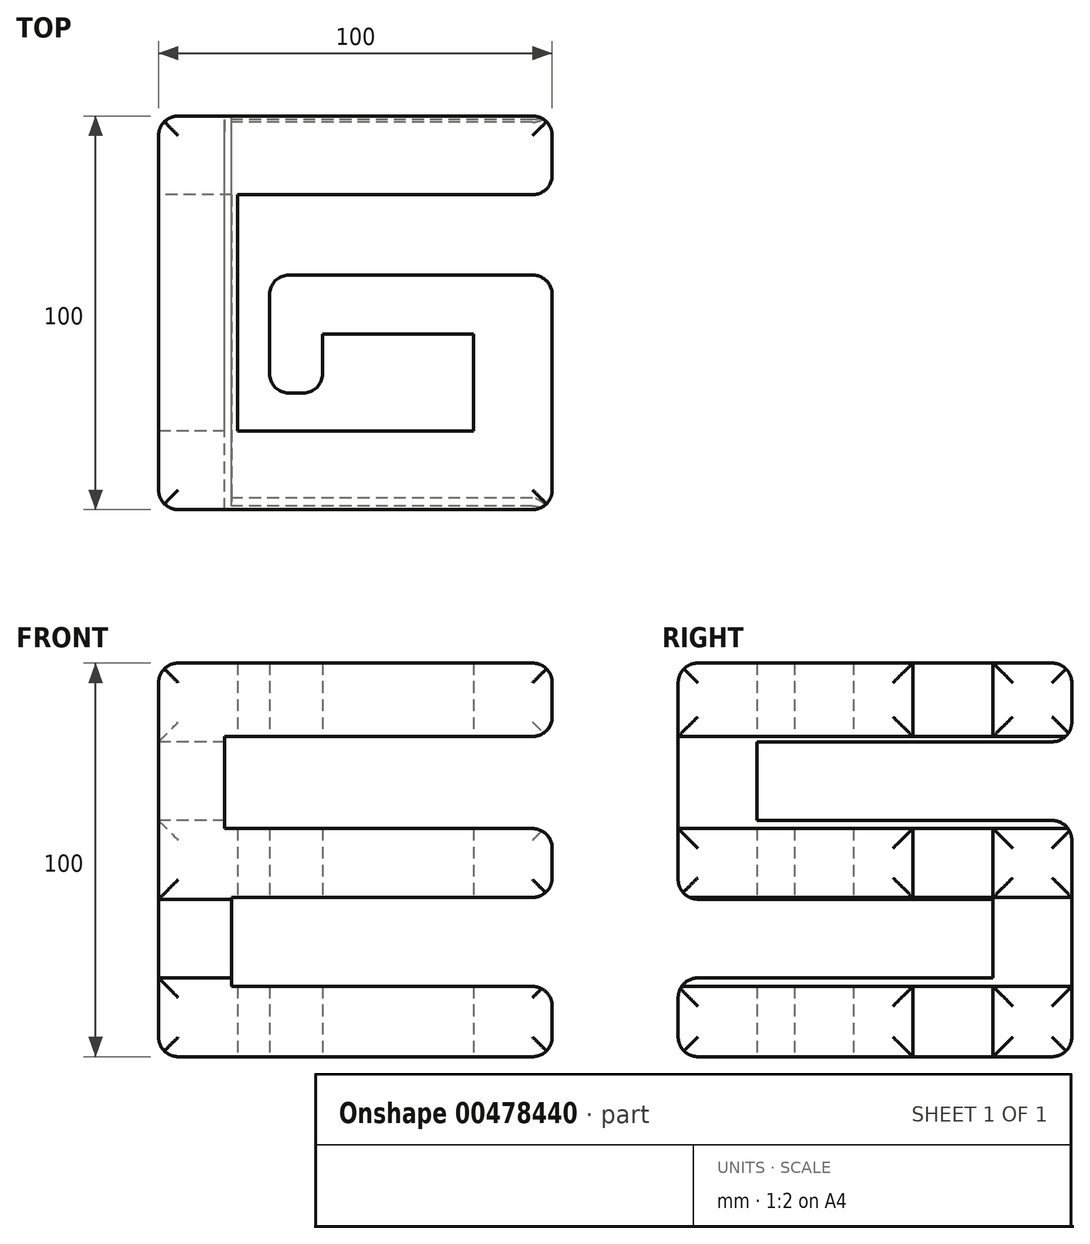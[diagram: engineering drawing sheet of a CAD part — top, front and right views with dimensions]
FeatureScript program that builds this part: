
annotation { "Feature Type Name" : "Feature", "Feature Type Description" : "" }
export const myFeature = defineFeature(function(context is Context, id is Id, definition is map)
    precondition{}
    {
        {
            var Q0;
            Q0=qCreatedBy(makeId("Top.planeOp"),FACE);
            var sketch = newSketch(context, id + "F0", { "sketchPlane" : qUnion([Q0])});
            skLineSegment(sketch, "E0.bottom", {"start": v(50, 50) * mm, "end": v(-50, 50) * mm, "construction": true});
            skLineSegment(sketch, "E0.top", {"start": v(50, -50) * mm, "end": v(-50, -50) * mm, "construction": true});
            skLineSegment(sketch, "E0.left", {"start": v(50, 50) * mm, "end": v(50, -50) * mm, "construction": true});
            skLineSegment(sketch, "E0.right", {"start": v(-50, 50) * mm, "end": v(-50, -50) * mm, "construction": true});
            skPoint(sketch, "E0.middle", {"position": v(0, 0) * mm});
            skLineSegment(sketch, "E1", {"start": v(45, 30) * mm, "end": v(-30, 30) * mm});
            skLineSegment(sketch, "E2", {"start": v(-30, 30) * mm, "end": v(-30, -30) * mm});
            skLineSegment(sketch, "E3", {"start": v(-30, -30) * mm, "end": v(30, -30) * mm});
            skLineSegment(sketch, "E4", {"start": v(30, -30) * mm, "end": v(30, -5.42) * mm});
            skLineSegment(sketch, "E5", {"start": v(-16.82, 9.58) * mm, "end": v(45, 9.58) * mm});
            skLineSegment(sketch, "E6", {"start": v(50, 4.58) * mm, "end": v(50, -45) * mm});
            skLineSegment(sketch, "E7", {"start": v(45, -50) * mm, "end": v(-45, -50) * mm});
            skLineSegment(sketch, "E8", {"start": v(-50, -45) * mm, "end": v(-50, 45) * mm});
            skLineSegment(sketch, "E9", {"start": v(-45, 50) * mm, "end": v(45, 50) * mm});
            skLineSegment(sketch, "E10", {"start": v(50, 45) * mm, "end": v(50, 35) * mm});
            skPoint(sketch, "E11.orphan", {"position": v(30, 0) * mm});
            skPoint(sketch, "E12.start.orphan", {"position": v(-13.97, 0) * mm});
            skPoint(sketch, "E13.visualSharp", {"position": v(-50, 50) * mm});
            skArc(sketch, "E13.filletArc", {"start": v(-45, 50) * mm, "mid": v(-48.54, 48.54) * mm, "end": v(-50, 45) * mm});
            skPoint(sketch, "E14.visualSharp", {"position": v(50, 50) * mm});
            skArc(sketch, "E14.filletArc", {"start": v(50, 45) * mm, "mid": v(48.54, 48.54) * mm, "end": v(45, 50) * mm});
            skPoint(sketch, "E15.visualSharp", {"position": v(50, 9.58) * mm});
            skArc(sketch, "E15.filletArc", {"start": v(50, 4.58) * mm, "mid": v(48.54, 8.12) * mm, "end": v(45, 9.58) * mm});
            skPoint(sketch, "E16.visualSharp", {"position": v(-21.82, 9.58) * mm});
            skArc(sketch, "E16.filletArc", {"start": v(-16.82, 9.58) * mm, "mid": v(-20.36, 8.12) * mm, "end": v(-21.82, 4.58) * mm});
            skPoint(sketch, "E17.visualSharp", {"position": v(-21.82, -5.42) * mm});
            skPoint(sketch, "E18.visualSharp", {"position": v(50, -50) * mm});
            skArc(sketch, "E18.filletArc", {"start": v(45, -50) * mm, "mid": v(48.54, -48.54) * mm, "end": v(50, -45) * mm});
            skPoint(sketch, "E19.visualSharp", {"position": v(-50, -50) * mm});
            skArc(sketch, "E19.filletArc", {"start": v(-50, -45) * mm, "mid": v(-48.54, -48.54) * mm, "end": v(-45, -50) * mm});
            skPoint(sketch, "E20.visualSharp", {"position": v(50, 30) * mm});
            skArc(sketch, "E20.filletArc", {"start": v(45, 30) * mm, "mid": v(48.54, 31.46) * mm, "end": v(50, 35) * mm});
            skLineSegment(sketch, "E21", {"start": v(-21.82, 4.58) * mm, "end": v(-21.82, -15.42) * mm});
            skLineSegment(sketch, "E22", {"start": v(-16.82, -20.42) * mm, "end": v(-13.33, -20.42) * mm});
            skLineSegment(sketch, "E23", {"start": v(-8.33, -15.42) * mm, "end": v(-8.33, -5.42) * mm});
            skLineSegment(sketch, "E24", {"start": v(-8.33, -5.42) * mm, "end": v(30, -5.42) * mm});
            skPoint(sketch, "E25.visualSharp", {"position": v(-21.82, -20.42) * mm});
            skArc(sketch, "E25.filletArc", {"start": v(-21.82, -15.42) * mm, "mid": v(-20.36, -18.95) * mm, "end": v(-16.82, -20.42) * mm});
            skPoint(sketch, "E26.visualSharp", {"position": v(-8.33, -20.42) * mm});
            skArc(sketch, "E26.filletArc", {"start": v(-13.33, -20.42) * mm, "mid": v(-9.8, -18.95) * mm, "end": v(-8.33, -15.42) * mm});
            skSolve(sketch);
        }
        {
            var Q0;
            Q0=qCreatedBy(makeId("Front.planeOp"),FACE);
            var sketch = newSketch(context, id + "F1", { "sketchPlane" : qUnion([Q0])});
            skLineSegment(sketch, "E27.bottom", {"start": v(50, 50) * mm, "end": v(-50, 50) * mm, "construction": true});
            skLineSegment(sketch, "E27.top", {"start": v(50, -50) * mm, "end": v(-50, -50) * mm, "construction": true});
            skLineSegment(sketch, "E27.right", {"start": v(-50, 50) * mm, "end": v(-50, -50) * mm, "construction": true});
            skPoint(sketch, "E27.middle", {"position": v(0, 0) * mm});
            skLineSegment(sketch, "E28", {"start": v(-33.2, 31.36) * mm, "end": v(45, 31.36) * mm});
            skLineSegment(sketch, "E29", {"start": v(-33.2, 31.36) * mm, "end": v(-33.2, 7.95) * mm});
            skLineSegment(sketch, "E30", {"start": v(-33.2, 7.95) * mm, "end": v(45, 7.95) * mm});
            skLineSegment(sketch, "E31", {"start": v(-31.42, -9.54) * mm, "end": v(45, -9.54) * mm});
            skLineSegment(sketch, "E32", {"start": v(-31.42, -9.54) * mm, "end": v(-31.42, -32.16) * mm});
            skLineSegment(sketch, "E33", {"start": v(-31.42, -32.16) * mm, "end": v(45, -32.16) * mm});
            skLineSegment(sketch, "E34", {"start": v(50, 36.36) * mm, "end": v(50, 45) * mm});
            skLineSegment(sketch, "E35", {"start": v(45, 50) * mm, "end": v(-45, 50) * mm});
            skLineSegment(sketch, "E36", {"start": v(-50, 45) * mm, "end": v(-50, -45) * mm});
            skLineSegment(sketch, "E37", {"start": v(-45, -50) * mm, "end": v(45, -50) * mm});
            skLineSegment(sketch, "E38", {"start": v(50, -45) * mm, "end": v(50, -37.16) * mm});
            skLineSegment(sketch, "E39", {"start": v(50, 2.95) * mm, "end": v(50, -4.54) * mm});
            skLineSegment(sketch, "E40.trimOffspring", {"start": v(50, 7.95) * mm, "end": v(50, -9.54) * mm, "construction": true});
            skPoint(sketch, "E41.visualSharp", {"position": v(-50, 50) * mm});
            skArc(sketch, "E41.filletArc", {"start": v(-45, 50) * mm, "mid": v(-48.54, 48.54) * mm, "end": v(-50, 45) * mm});
            skPoint(sketch, "E42.visualSharp", {"position": v(50, 50) * mm});
            skArc(sketch, "E42.filletArc", {"start": v(50, 45) * mm, "mid": v(48.54, 48.54) * mm, "end": v(45, 50) * mm});
            skPoint(sketch, "E43.visualSharp", {"position": v(50, 31.36) * mm});
            skArc(sketch, "E43.filletArc", {"start": v(45, 31.36) * mm, "mid": v(48.54, 32.83) * mm, "end": v(50, 36.36) * mm});
            skPoint(sketch, "E44.visualSharp", {"position": v(50, 7.95) * mm});
            skArc(sketch, "E44.filletArc", {"start": v(50, 2.95) * mm, "mid": v(48.54, 6.49) * mm, "end": v(45, 7.95) * mm});
            skPoint(sketch, "E45.visualSharp", {"position": v(50, -9.54) * mm});
            skArc(sketch, "E45.filletArc", {"start": v(45, -9.54) * mm, "mid": v(48.54, -8.07) * mm, "end": v(50, -4.54) * mm});
            skPoint(sketch, "E46.visualSharp", {"position": v(50, -32.16) * mm});
            skArc(sketch, "E46.filletArc", {"start": v(50, -37.16) * mm, "mid": v(48.54, -33.63) * mm, "end": v(45, -32.16) * mm});
            skPoint(sketch, "E47.visualSharp", {"position": v(50, -50) * mm});
            skArc(sketch, "E47.filletArc", {"start": v(45, -50) * mm, "mid": v(48.54, -48.54) * mm, "end": v(50, -45) * mm});
            skPoint(sketch, "E48.visualSharp", {"position": v(-50, -50) * mm});
            skArc(sketch, "E48.filletArc", {"start": v(-50, -45) * mm, "mid": v(-48.54, -48.54) * mm, "end": v(-45, -50) * mm});
            skSolve(sketch);
        }
        {
            var Q0;
            Q0=qCreatedBy(makeId("Right.planeOp"),FACE);
            var sketch = newSketch(context, id + "F2", { "sketchPlane" : qUnion([Q0])});
            skLineSegment(sketch, "E49.bottom", {"start": v(50, 50) * mm, "end": v(-50, 50) * mm, "construction": true});
            skLineSegment(sketch, "E49.top", {"start": v(50, -50) * mm, "end": v(-50, -50) * mm, "construction": true});
            skPoint(sketch, "E49.middle", {"position": v(0, 0) * mm});
            skLineSegment(sketch, "E50", {"start": v(-50, 45) * mm, "end": v(-50, -5) * mm});
            skLineSegment(sketch, "E51", {"start": v(-50, -35) * mm, "end": v(-50, -45) * mm});
            skLineSegment(sketch, "E52", {"start": v(-45, -50) * mm, "end": v(45, -50) * mm});
            skLineSegment(sketch, "E53", {"start": v(50, -45) * mm, "end": v(50, 5) * mm});
            skLineSegment(sketch, "E54", {"start": v(45, 10) * mm, "end": v(-30, 10) * mm});
            skLineSegment(sketch, "E55", {"start": v(-30, 10) * mm, "end": v(-30, 30) * mm});
            skLineSegment(sketch, "E56", {"start": v(-30, 30) * mm, "end": v(45, 30) * mm});
            skLineSegment(sketch, "E57", {"start": v(50, 45) * mm, "end": v(50, 35) * mm});
            skLineSegment(sketch, "E58", {"start": v(45, 50) * mm, "end": v(-45, 50) * mm});
            skLineSegment(sketch, "E59", {"start": v(-45, -10) * mm, "end": v(30, -10) * mm});
            skLineSegment(sketch, "E60", {"start": v(30, -10) * mm, "end": v(30, -30) * mm});
            skLineSegment(sketch, "E61", {"start": v(30, -30) * mm, "end": v(-45, -30) * mm});
            skPoint(sketch, "E62.visualSharp", {"position": v(-50, 50) * mm});
            skArc(sketch, "E62.filletArc", {"start": v(-45, 50) * mm, "mid": v(-48.54, 48.54) * mm, "end": v(-50, 45) * mm});
            skPoint(sketch, "E63.visualSharp", {"position": v(50, 50) * mm});
            skArc(sketch, "E63.filletArc", {"start": v(50, 45) * mm, "mid": v(48.54, 48.54) * mm, "end": v(45, 50) * mm});
            skPoint(sketch, "E64.visualSharp", {"position": v(50, 30) * mm});
            skArc(sketch, "E64.filletArc", {"start": v(45, 30) * mm, "mid": v(48.54, 31.46) * mm, "end": v(50, 35) * mm});
            skPoint(sketch, "E65.visualSharp", {"position": v(-50, -10) * mm});
            skArc(sketch, "E65.filletArc", {"start": v(-50, -5) * mm, "mid": v(-48.54, -8.54) * mm, "end": v(-45, -10) * mm});
            skPoint(sketch, "E66.visualSharp", {"position": v(-50, -30) * mm});
            skArc(sketch, "E66.filletArc", {"start": v(-45, -30) * mm, "mid": v(-48.54, -31.46) * mm, "end": v(-50, -35) * mm});
            skPoint(sketch, "E67.visualSharp", {"position": v(-50, -50) * mm});
            skArc(sketch, "E67.filletArc", {"start": v(-50, -45) * mm, "mid": v(-48.54, -48.54) * mm, "end": v(-45, -50) * mm});
            skPoint(sketch, "E68.visualSharp", {"position": v(50, -50) * mm});
            skArc(sketch, "E68.filletArc", {"start": v(45, -50) * mm, "mid": v(48.54, -48.54) * mm, "end": v(50, -45) * mm});
            skPoint(sketch, "E69.visualSharp", {"position": v(50, 10) * mm});
            skArc(sketch, "E69.filletArc", {"start": v(50, 5) * mm, "mid": v(48.54, 8.54) * mm, "end": v(45, 10) * mm});
            skSolve(sketch);
        }
        {
            var Q0;
            Q0 = qSketchRegion(id + "F0", true);
            extrude(context, id + "F3", {"entities" : qUnion([Q0]), "endBound" : BoundingType.SYMMETRIC, "depth" : 100 * mm});
        }
        {
            var Q0;
            Q0 = qSketchRegion(id + "F1", true);
            extrude(context, id + "F4", {"entities" : qUnion([Q0]), "operationType" : NewBodyOperationType.INTERSECT, "endBound" : BoundingType.SYMMETRIC, "depth" : 100 * mm});
        }
        {
            var Q0;
            Q0 = qSketchRegion(id + "F2", true);
            extrude(context, id + "F5", {"entities" : qUnion([Q0]), "operationType" : NewBodyOperationType.INTERSECT, "endBound" : BoundingType.SYMMETRIC, "depth" : 100 * mm});
        }
    });
